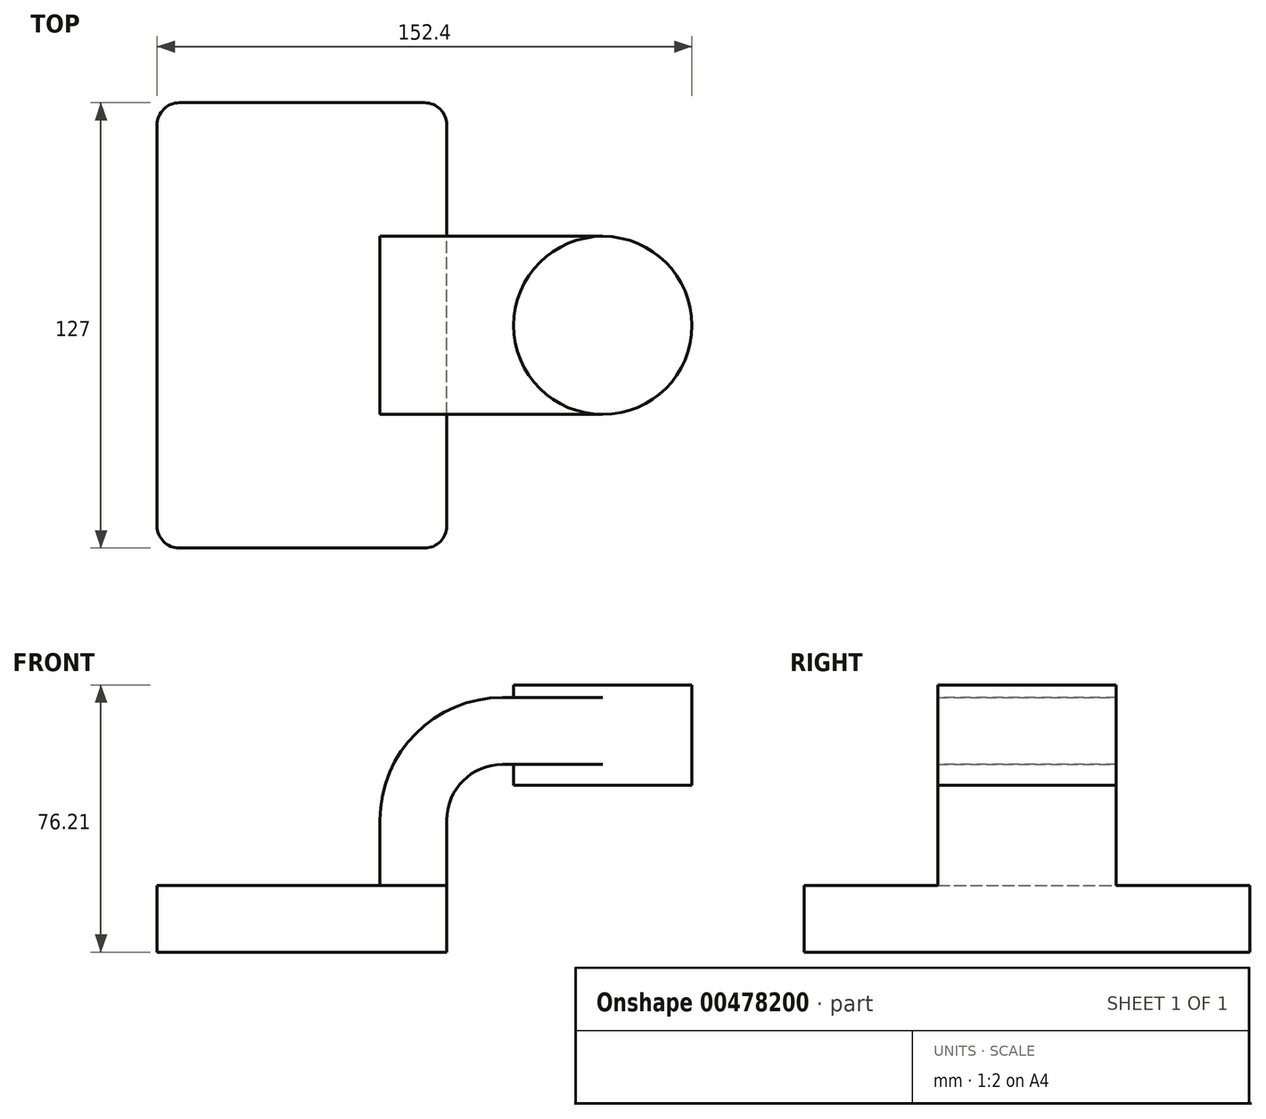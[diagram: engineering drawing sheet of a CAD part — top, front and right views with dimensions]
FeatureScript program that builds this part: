
annotation { "Feature Type Name" : "Feature", "Feature Type Description" : "" }
export const myFeature = defineFeature(function(context is Context, id is Id, definition is map)
    precondition{}
    {
        {
            var Q0;
            Q0=qCreatedBy(makeId("Front.planeOp"),FACE);
            var sketch = newSketch(context, id + "F0", { "sketchPlane" : qUnion([Q0])});
            skLineSegment(sketch, "E0.bottom", {"start": v(41.27, 9.53) * mm, "end": v(-41.28, 9.53) * mm});
            skLineSegment(sketch, "E0.top", {"start": v(41.28, -9.52) * mm, "end": v(-41.27, -9.52) * mm});
            skLineSegment(sketch, "E0.left", {"start": v(41.28, 9.53) * mm, "end": v(41.28, -9.52) * mm});
            skLineSegment(sketch, "E0.right", {"start": v(-41.28, 9.53) * mm, "end": v(-41.27, -9.52) * mm});
            skPoint(sketch, "E0.middle", {"position": v(0, 0) * mm});
            skLineSegment(sketch, "E1.bottom", {"start": v(60.32, 38.1) * mm, "end": v(111.12, 38.1) * mm});
            skLineSegment(sketch, "E1.top", {"start": v(60.32, 66.68) * mm, "end": v(111.12, 66.68) * mm});
            skLineSegment(sketch, "E1.left", {"start": v(60.32, 38.1) * mm, "end": v(60.32, 66.68) * mm});
            skLineSegment(sketch, "E1.right", {"start": v(111.13, 38.1) * mm, "end": v(111.13, 66.68) * mm});
            skPoint(sketch, "E1.middle", {"position": v(85.73, 52.39) * mm});
            skLineSegment(sketch, "E2", {"start": v(41.27, 9.53) * mm, "end": v(41.27, 28.14) * mm});
            skLineSegment(sketch, "E3", {"start": v(85.72, 66.68) * mm, "end": v(85.72, 38.1) * mm});
            skArc(sketch, "E4", {"start": v(41.27, 28.14) * mm, "mid": v(45.92, 39.36) * mm, "end": v(57.15, 44.01) * mm});
            skLineSegment(sketch, "E5", {"start": v(57.15, 44.01) * mm, "end": v(85.72, 44.01) * mm});
            skLineSegment(sketch, "E6.0", {"start": v(57.15, 63.06) * mm, "end": v(85.72, 63.06) * mm});
            skArc(sketch, "E6.1", {"start": v(22.22, 28.14) * mm, "mid": v(32.45, 52.83) * mm, "end": v(57.15, 63.06) * mm});
            skLineSegment(sketch, "E6.2", {"start": v(22.22, 9.53) * mm, "end": v(22.22, 28.14) * mm});
            skFitSpline(sketch, "E7", {"points": [v(57.15, 63.06) * mm, v(-41.28, 9.53) * mm], "startDerivative": vector(-125.91, 11.15) * mm, "endDerivative": vector(-68.63, -134.5) * mm});
            skSolve(sketch);
        }
        {
            var Q0;
            Q0=makeQuery(id+"F0.imprint","IMPRINT",FACE,{"disambiguationData":[TD([[makeQuery(id+"F0.imprint","IMPRINT",EDGE,{"derivedFrom":sQuery(id+"F0.wireOp",EDGE,"E0.top")}),-1.0]])]});
            extrude(context, id + "F1", {"entities" : qUnion([Q0]), "endBound" : BoundingType.SYMMETRIC, "depth" : 127 * mm});
        }
        {
            var Q0;
            {var subQ1=sQuery(id+"F0.wireOp",EDGE,"E2");Q0=makeQuery(id+"F0.imprint","IMPRINT",FACE,{"disambiguationData":[TD([[makeQuery(id+"F0.imprint","IMPRINT",EDGE,{"derivedFrom":subQ1}),1.0]])]});}
            var Q1;
            {var subQ0=sQuery(id+"F0.wireOp",EDGE,"E5");var subQ1=sQuery(id+"F0.wireOp",EDGE,"E1.left");var subQ2=makeQuery(id+"F0.imprint","INTERSECT",VERTEX,{"derivedFrom":[subQ1,subQ0]});Q1=makeQuery(id+"F0.imprint","IMPRINT",FACE,{"disambiguationData":[TD([[makeQuery(id+"F0.imprint","IMPRINT",EDGE,{"disambiguationData":[TD([[subQ2,-1.0]])],"derivedFrom":subQ1}),-1.0]])]});}
            extrude(context, id + "F2", {"entities" : qUnion([Q0, Q1]), "operationType" : NewBodyOperationType.ADD, "endBound" : BoundingType.SYMMETRIC, "depth" : 50.8 * mm});
        }
        {
            var Q0;
            Q0=makeQuery(id+"F0.imprint","IMPRINT",FACE,{"disambiguationData":[TD([[makeQuery(id+"F0.imprint","IMPRINT",EDGE,{"derivedFrom":sQuery(id+"F0.wireOp",EDGE,"E6.1")}),1.0]])]});
            extrude(context, id + "F3", {"entities" : qUnion([Q0]), "operationType" : NewBodyOperationType.ADD, "endBound" : BoundingType.SYMMETRIC, "depth" : 12.7 * mm});
        }
        {
            var Q0;
            {var subQ4=sQuery(id+"F0.wireOp",EDGE,"E1.right");Q0=makeQuery(id+"F0.imprint","IMPRINT",FACE,{"disambiguationData":[TD([[makeQuery(id+"F0.imprint","IMPRINT",EDGE,{"derivedFrom":subQ4}),1.0]])]});}
            var Q1;
            Q1=sQuery(id+"F0.wireOp",EDGE,"E3");
            revolve(context, id + "F4", {"operationType" : NewBodyOperationType.ADD, "entities" : qUnion([Q0]), "axis" : qUnion([Q1]), "revolveType" : RevolveType.FULL});
        }
        {
            var Q0;
            Q0=makeQuery(id+"F1.opExtrude","CAP_EDGE",EDGE,{"disambiguationData":[OSD([sQuery(id+"F0.wireOp",EDGE,"E0.right")])],"isStart":false});
            var Q1;
            Q1=makeQuery(id+"F1.opExtrude","CAP_EDGE",EDGE,{"disambiguationData":[OSD([sQuery(id+"F0.wireOp",EDGE,"E0.right")])],"isStart":true});
            var Q2;
            Q2=makeQuery(id+"F1.opExtrude","CAP_EDGE",EDGE,{"disambiguationData":[OSD([sQuery(id+"F0.wireOp",EDGE,"E0.left")])],"isStart":false});
            var Q3;
            Q3=makeQuery(id+"F1.opExtrude","CAP_EDGE",EDGE,{"disambiguationData":[OSD([sQuery(id+"F0.wireOp",EDGE,"E0.left")])],"isStart":true});
            fillet(context, id + "F5", {"entities" : qUnion([Q0, Q1, Q2, Q3]), "radius" : 6.35 * mm, "tangentPropagation" : true, "allowEdgeOverflow" : false});
        }
    });
